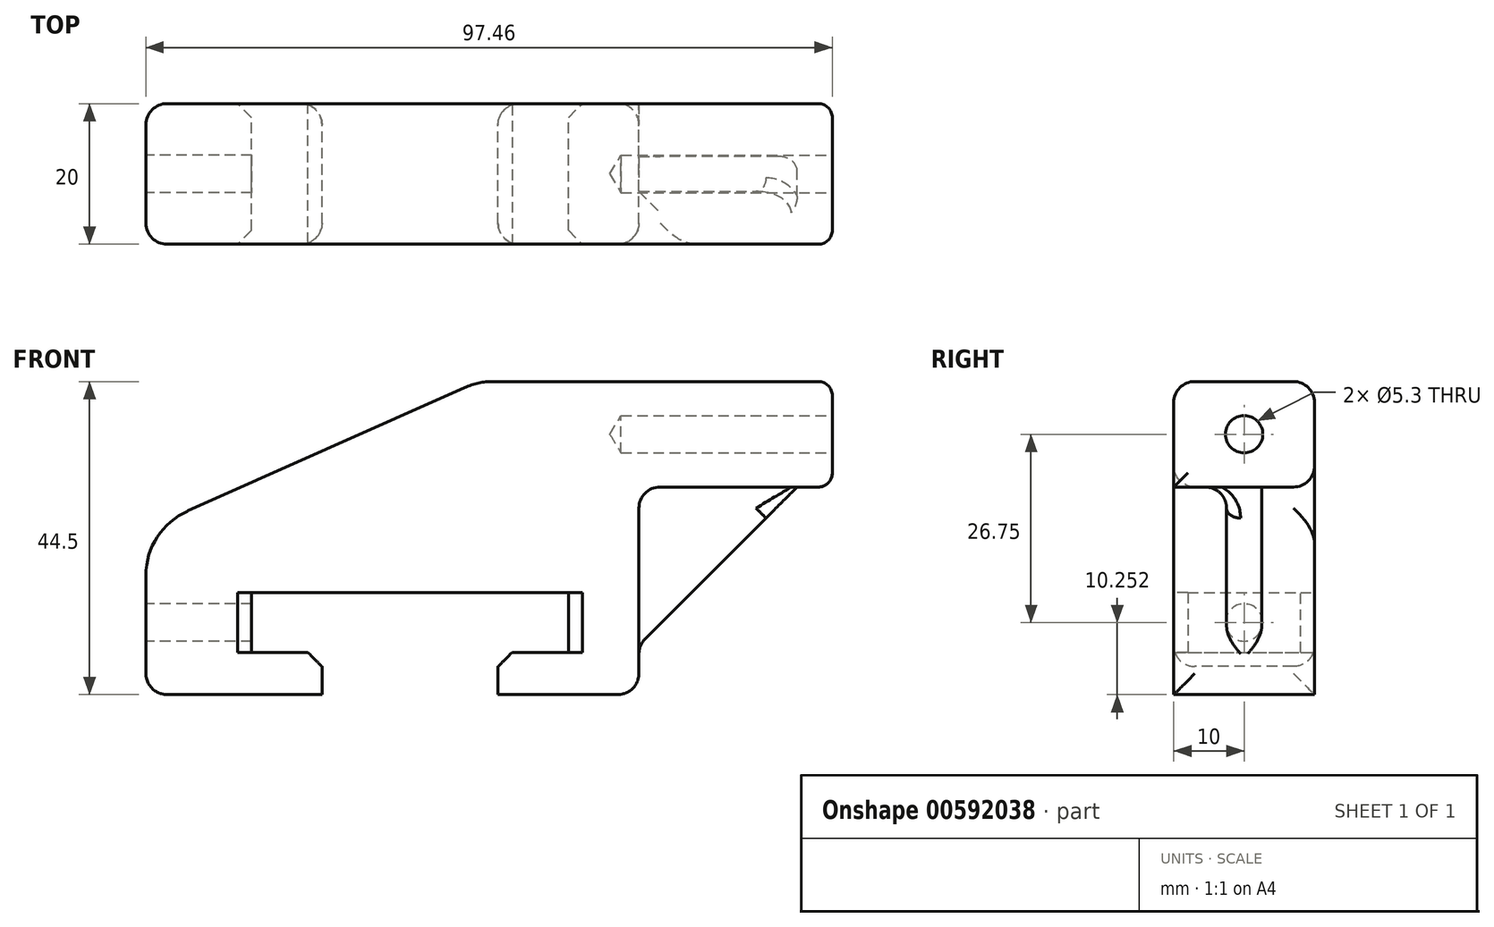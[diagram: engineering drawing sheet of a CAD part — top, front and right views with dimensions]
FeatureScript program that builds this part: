
annotation { "Feature Type Name" : "Feature", "Feature Type Description" : "" }
export const myFeature = defineFeature(function(context is Context, id is Id, definition is map)
    precondition{}
    {
        {
            var Q0;
            Q0=qCreatedBy(makeId("Front.planeOp"),FACE);
            var sketch = newSketch(context, id + "F0", { "sketchPlane" : qUnion([Q0])});
            skLineSegment(sketch, "E0", {"start": v(-69.54, -2.42) * mm, "end": v(-69.54, -25.86) * mm});
            skLineSegment(sketch, "E1", {"start": v(-69.54, -25.86) * mm, "end": v(-44.54, -25.86) * mm});
            skLineSegment(sketch, "E2", {"start": v(-44.54, -25.86) * mm, "end": v(-44.54, -19.86) * mm});
            skLineSegment(sketch, "E3", {"start": v(-44.54, -19.86) * mm, "end": v(-54.54, -19.86) * mm});
            skLineSegment(sketch, "E4", {"start": v(-54.54, -19.86) * mm, "end": v(-54.54, -11.36) * mm});
            skLineSegment(sketch, "E5", {"start": v(-54.54, -11.36) * mm, "end": v(-44.54, -11.36) * mm});
            skLineSegment(sketch, "E6", {"start": v(-44.54, -11.36) * mm, "end": v(-9.54, -11.36) * mm});
            skLineSegment(sketch, "E7", {"start": v(-9.54, -11.36) * mm, "end": v(-9.54, -19.86) * mm});
            skLineSegment(sketch, "E8", {"start": v(-9.54, -19.86) * mm, "end": v(-19.54, -19.86) * mm});
            skLineSegment(sketch, "E9", {"start": v(-19.54, -19.86) * mm, "end": v(-19.54, -25.86) * mm});
            skLineSegment(sketch, "E10", {"start": v(-19.54, -25.86) * mm, "end": v(0.46, -25.86) * mm});
            skLineSegment(sketch, "E11", {"start": v(0.46, -25.86) * mm, "end": v(0.46, 3.64) * mm});
            skLineSegment(sketch, "E12", {"start": v(0.46, 3.64) * mm, "end": v(22.92, 3.64) * mm});
            skLineSegment(sketch, "E13", {"start": v(22.92, 3.64) * mm, "end": v(22.92, 18.64) * mm});
            skLineSegment(sketch, "E14", {"start": v(22.92, 18.64) * mm, "end": v(-22.34, 18.64) * mm});
            skLineSegment(sketch, "E15", {"start": v(-80.76, -15.6) * mm, "end": v(-46.79, -15.6) * mm, "construction": true});
            skPoint(sketch, "E15.startSnap0", {"position": v(-54.54, -15.6) * mm});
            skLineSegment(sketch, "E16", {"start": v(26.63, 11.14) * mm, "end": v(-61.45, 11.14) * mm, "construction": true});
            skPoint(sketch, "E17", {"position": v(-69.54, -2.42) * mm});
            skPoint(sketch, "E18", {"position": v(-22.34, 18.64) * mm});
            skLineSegment(sketch, "E19", {"start": v(-69.54, -2.42) * mm, "end": v(-22.34, 18.64) * mm});
            skSolve(sketch);
        }
        {
            var Q0;
            Q0=makeQuery(id+"F0.imprint","IMPRINT",FACE,{"disambiguationData":[TD([[makeQuery(id+"F0.imprint","IMPRINT",EDGE,{"derivedFrom":sQuery(id+"F0.wireOp",EDGE,"E0")}),1.0]])]});
            extrude(context, id + "F1", {"entities" : qUnion([Q0]), "endBound" : BoundingType.SYMMETRIC, "depth" : 20 * mm, "offsetDistance" : 25 * mm});
        }
        {
            var Q0;
            Q0=makeQuery(id+"F1.opExtrude","SWEPT_FACE",FACE,{"disambiguationData":[OSD([sQuery(id+"F0.wireOp",EDGE,"E0")])]});
            var sketch = newSketch(context, id + "F2", { "sketchPlane" : qUnion([Q0])});
            skPoint(sketch, "E20", {"position": v(0, -15.6) * mm});
            skSolve(sketch);
        }
        {
            var Q0;
            Q0=makeQuery(id+"F1.opExtrude","SWEPT_FACE",FACE,{"disambiguationData":[OSD([sQuery(id+"F0.wireOp",EDGE,"E13")])]});
            var sketch = newSketch(context, id + "F3", { "sketchPlane" : qUnion([Q0])});
            skPoint(sketch, "E21", {"position": v(0, 11.14) * mm});
            skSolve(sketch);
        }
        {
            var Q0;
            Q0=sQuery(id+"F3.wireOp",VERTEX,"E21");
            var Q1;
            Q1=makeQuery(id+"F1.opExtrude","SWEPT_BODY",BODY,{"disambiguationData":[OSD([sQuery(id+"F0.wireOp",EDGE,"E0"),sQuery(id+"F0.wireOp",EDGE,"E1"),sQuery(id+"F0.wireOp",EDGE,"E2"),sQuery(id+"F0.wireOp",EDGE,"E3"),sQuery(id+"F0.wireOp",EDGE,"E4"),sQuery(id+"F0.wireOp",EDGE,"E5"),sQuery(id+"F0.wireOp",EDGE,"E6"),sQuery(id+"F0.wireOp",EDGE,"E7"),sQuery(id+"F0.wireOp",EDGE,"E8"),sQuery(id+"F0.wireOp",EDGE,"E9"),sQuery(id+"F0.wireOp",EDGE,"E10"),sQuery(id+"F0.wireOp",EDGE,"E11"),sQuery(id+"F0.wireOp",EDGE,"E12"),sQuery(id+"F0.wireOp",EDGE,"E13"),sQuery(id+"F0.wireOp",EDGE,"E14"),sQuery(id+"F0.wireOp",EDGE,"E19")])]});
            hole(context, id + "F4", {"style" : HoleStyle.SIMPLE, "endStyle" : HoleEndStyle.BLIND, "holeDiameter" : 5.3 * mm, "majorDiameter" : 5 * mm, "holeDepth" : 25 * mm, "isTappedThrough" : true, "tappedDepth" : 12 * mm, "tapClearance" : 3, "locations" : qUnion([Q0]), "scope" : qUnion([Q1])});
        }
        {
            var Q0;
            Q0=sQuery(id+"F2.wireOp",VERTEX,"E20");
            var Q1;
            Q1=makeQuery(id+"F1.opExtrude","SWEPT_BODY",BODY,{"disambiguationData":[OSD([sQuery(id+"F0.wireOp",EDGE,"E0"),sQuery(id+"F0.wireOp",EDGE,"E1"),sQuery(id+"F0.wireOp",EDGE,"E2"),sQuery(id+"F0.wireOp",EDGE,"E3"),sQuery(id+"F0.wireOp",EDGE,"E4"),sQuery(id+"F0.wireOp",EDGE,"E5"),sQuery(id+"F0.wireOp",EDGE,"E6"),sQuery(id+"F0.wireOp",EDGE,"E7"),sQuery(id+"F0.wireOp",EDGE,"E8"),sQuery(id+"F0.wireOp",EDGE,"E9"),sQuery(id+"F0.wireOp",EDGE,"E10"),sQuery(id+"F0.wireOp",EDGE,"E11"),sQuery(id+"F0.wireOp",EDGE,"E12"),sQuery(id+"F0.wireOp",EDGE,"E13"),sQuery(id+"F0.wireOp",EDGE,"E14"),sQuery(id+"F0.wireOp",EDGE,"E19")])]});
            hole(context, id + "F5", {"style" : HoleStyle.SIMPLE, "endStyle" : HoleEndStyle.BLIND, "holeDiameter" : 5.3 * mm, "majorDiameter" : 5 * mm, "holeDepth" : 25 * mm, "isTappedThrough" : true, "tappedDepth" : 12 * mm, "tapClearance" : 3, "locations" : qUnion([Q0]), "scope" : qUnion([Q1])});
        }
        {
            var Q0;
            Q0=makeQuery(id+"F1.opExtrude","SWEPT_FACE",FACE,{"disambiguationData":[OSD([sQuery(id+"F0.wireOp",EDGE,"E12")])]});
            var sketch = newSketch(context, id + "F6", { "sketchPlane" : qUnion([Q0])});
            skLineSegment(sketch, "E22", {"start": v(0.46, 2.5) * mm, "end": v(22.92, 2.5) * mm});
            skLineSegment(sketch, "E23", {"start": v(22.92, 2.5) * mm, "end": v(22.92, -2.5) * mm});
            skLineSegment(sketch, "E24", {"start": v(22.92, -2.5) * mm, "end": v(0.46, -2.5) * mm});
            skLineSegment(sketch, "E25", {"start": v(0.46, -2.5) * mm, "end": v(0.46, 2.5) * mm});
            skSolve(sketch);
        }
        {
            var Q0;
            Q0=makeQuery(id+"F6.imprint","IMPRINT",FACE,{"disambiguationData":[TD([[makeQuery(id+"F6.imprint","IMPRINT",EDGE,{"derivedFrom":sQuery(id+"F6.wireOp",EDGE,"E22")}),-1.0]])]});
            extrude(context, id + "F7", {"entities" : qUnion([Q0]), "operationType" : NewBodyOperationType.ADD, "depth" : 29 * mm, "offsetDistance" : 25 * mm});
        }
        {
            var Q0;
            Q0=makeQuery(id+"F7.opExtrude","CAP_EDGE",EDGE,{"disambiguationData":[OSD([sQuery(id+"F6.wireOp",EDGE,"E23")])],"isStart":false});
            chamfer(context, id + "F8", {"entities" : qUnion([Q0]), "chamferType" : ChamferType.TWO_OFFSETS, "width1" : 29 * mm, "oppositeDirection" : false, "width2" : 29 * mm, "tangentPropagation" : true});
        }
        {
            var Q0;
            {var subQ0=sQuery(id+"F0.wireOp",EDGE,"E12");var subQ1=sQuery(id+"F0.wireOp",EDGE,"E11");Q0=makeQuery(id+"F7.boolean.opBoolean","SPLIT",EDGE,{"disambiguationData":[TD([makeQuery(id+"F7.opExtrude","SWEPT_FACE",FACE,{"disambiguationData":[OSD([sQuery(id+"F6.wireOp",EDGE,"E24")])]})])],"derivedFrom":makeQuery(id+"F1.opExtrude","SWEPT_EDGE",EDGE,{"disambiguationData":[OSD([subQ1,subQ0])]})});}
            var Q1;
            {var subQ0=sQuery(id+"F0.wireOp",EDGE,"E12");var subQ1=sQuery(id+"F0.wireOp",EDGE,"E11");Q1=makeQuery(id+"F7.boolean.opBoolean","SPLIT",EDGE,{"disambiguationData":[TD([makeQuery(id+"F7.opExtrude","SWEPT_FACE",FACE,{"disambiguationData":[OSD([sQuery(id+"F6.wireOp",EDGE,"E22")])]})])],"derivedFrom":makeQuery(id+"F1.opExtrude","SWEPT_EDGE",EDGE,{"disambiguationData":[OSD([subQ1,subQ0])]})});}
            var Q2;
            Q2=makeQuery(id+"F7.opExtrude","SWEPT_EDGE",EDGE,{"disambiguationData":[OSD([sQuery(id+"F0.wireOp",EDGE,"E11"),sQuery(id+"F0.wireOp",EDGE,"E12"),sQuery(id+"F6.wireOp",EDGE,"E22"),sQuery(id+"F6.wireOp",EDGE,"E25")])]});
            var Q3;
            Q3=makeQuery(id+"F7.opExtrude","CAP_EDGE",EDGE,{"disambiguationData":[OSD([sQuery(id+"F6.wireOp",EDGE,"E22")])],"isStart":true});
            var Q4;
            Q4=makeQuery(id+"F7.opExtrude","CAP_EDGE",EDGE,{"disambiguationData":[OSD([sQuery(id+"F6.wireOp",EDGE,"E24")])],"isStart":true});
            var Q5;
            Q5=makeQuery(id+"F7.opExtrude","SWEPT_EDGE",EDGE,{"disambiguationData":[OSD([sQuery(id+"F0.wireOp",EDGE,"E11"),sQuery(id+"F0.wireOp",EDGE,"E12"),sQuery(id+"F6.wireOp",EDGE,"E24"),sQuery(id+"F6.wireOp",EDGE,"E25")])]});
            var Q6;
            Q6=makeQuery(id+"F8.opChamfer","BLEND_EDGE",EDGE,{"blendedFrom":[makeQuery(id+"F7.opExtrude","CAP_EDGE",EDGE,{"disambiguationData":[OSD([sQuery(id+"F6.wireOp",EDGE,"E23")])],"isStart":false}),makeQuery(id+"F1.opExtrude","SWEPT_FACE",FACE,{"disambiguationData":[OSD([sQuery(id+"F0.wireOp",EDGE,"E11")])]})],"blendedInto":[makeQuery(id+"F1.opExtrude","SWEPT_FACE",FACE,{"disambiguationData":[OSD([sQuery(id+"F0.wireOp",EDGE,"E11")])]})]});
            var Q7;
            Q7=makeQuery(id+"F1.opExtrude","CAP_EDGE",EDGE,{"disambiguationData":[OSD([sQuery(id+"F0.wireOp",EDGE,"E12")])],"isStart":true});
            var Q8;
            Q8=makeQuery(id+"F1.opExtrude","CAP_EDGE",EDGE,{"disambiguationData":[OSD([sQuery(id+"F0.wireOp",EDGE,"E11")])],"isStart":false});
            var Q9;
            Q9=makeQuery(id+"F1.opExtrude","CAP_EDGE",EDGE,{"disambiguationData":[OSD([sQuery(id+"F0.wireOp",EDGE,"E14")])],"isStart":true});
            var Q10;
            Q10=makeQuery(id+"F1.opExtrude","CAP_EDGE",EDGE,{"disambiguationData":[OSD([sQuery(id+"F0.wireOp",EDGE,"E19")])],"isStart":true});
            var Q11;
            Q11=makeQuery(id+"F1.opExtrude","CAP_EDGE",EDGE,{"disambiguationData":[OSD([sQuery(id+"F0.wireOp",EDGE,"E19")])],"isStart":false});
            var Q12;
            Q12=makeQuery(id+"F1.opExtrude","CAP_EDGE",EDGE,{"disambiguationData":[OSD([sQuery(id+"F0.wireOp",EDGE,"E14")])],"isStart":false});
            var Q13;
            Q13=makeQuery(id+"F1.opExtrude","CAP_EDGE",EDGE,{"disambiguationData":[OSD([sQuery(id+"F0.wireOp",EDGE,"E0")])],"isStart":false});
            var Q14;
            Q14=makeQuery(id+"F1.opExtrude","CAP_EDGE",EDGE,{"disambiguationData":[OSD([sQuery(id+"F0.wireOp",EDGE,"E0")])],"isStart":true});
            var Q15;
            Q15=makeQuery(id+"F1.opExtrude","SWEPT_EDGE",EDGE,{"disambiguationData":[OSD([sQuery(id+"F0.wireOp",EDGE,"E0"),sQuery(id+"F0.wireOp",EDGE,"E1")])]});
            var Q16;
            Q16=makeQuery(id+"F1.opExtrude","SWEPT_EDGE",EDGE,{"disambiguationData":[OSD([sQuery(id+"F0.wireOp",EDGE,"E10"),sQuery(id+"F0.wireOp",EDGE,"E11")])]});
            var Q17;
            Q17=makeQuery(id+"F1.opExtrude","CAP_EDGE",EDGE,{"disambiguationData":[OSD([sQuery(id+"F0.wireOp",EDGE,"E2")])],"isStart":false});
            var Q18;
            Q18=makeQuery(id+"F1.opExtrude","CAP_EDGE",EDGE,{"disambiguationData":[OSD([sQuery(id+"F0.wireOp",EDGE,"E9")])],"isStart":false});
            var Q19;
            Q19=makeQuery(id+"F1.opExtrude","CAP_EDGE",EDGE,{"disambiguationData":[OSD([sQuery(id+"F0.wireOp",EDGE,"E9")])],"isStart":true});
            var Q20;
            Q20=makeQuery(id+"F1.opExtrude","CAP_EDGE",EDGE,{"disambiguationData":[OSD([sQuery(id+"F0.wireOp",EDGE,"E2")])],"isStart":true});
            fillet(context, id + "F9", {"entities" : qUnion([Q0, Q1, Q2, Q3, Q4, Q5, Q6, Q7, Q8, Q9, Q10, Q11, Q12, Q13, Q14, Q15, Q16, Q17, Q18, Q19, Q20]), "radius" : 3 * mm, "tangentPropagation" : true, "allowEdgeOverflow" : false});
        }
        {
            var Q0;
            Q0=makeQuery(id+"F7.boolean.opBoolean","MERGE",FACE,{"derivedFrom":[makeQuery(id+"F1.opExtrude","SWEPT_FACE",FACE,{"disambiguationData":[OSD([sQuery(id+"F0.wireOp",EDGE,"E13")])]}),makeQuery(id+"F7.opExtrude","SWEPT_FACE",FACE,{"disambiguationData":[OSD([sQuery(id+"F6.wireOp",EDGE,"E23")])]})]});
            extrude(context, id + "F10", {"entities" : qUnion([Q0]), "operationType" : NewBodyOperationType.ADD, "depth" : 5 * mm, "offsetDistance" : 25 * mm});
        }
        {
            var Q0;
            Q0=makeQuery(id+"F8.opChamfer","BLEND_EDGE",EDGE,{"blendedFrom":[makeQuery(id+"F7.opExtrude","CAP_EDGE",EDGE,{"disambiguationData":[OSD([sQuery(id+"F6.wireOp",EDGE,"E23")])],"isStart":false}),makeQuery(id+"F7.opExtrude","SWEPT_FACE",FACE,{"disambiguationData":[OSD([sQuery(id+"F6.wireOp",EDGE,"E24")])]})],"blendedInto":[makeQuery(id+"F7.opExtrude","SWEPT_FACE",FACE,{"disambiguationData":[OSD([sQuery(id+"F6.wireOp",EDGE,"E24")])]})]});
            var Q1;
            Q1=makeQuery(id+"F8.opChamfer","BLEND_EDGE",EDGE,{"blendedFrom":[makeQuery(id+"F7.opExtrude","CAP_EDGE",EDGE,{"disambiguationData":[OSD([sQuery(id+"F6.wireOp",EDGE,"E23")])],"isStart":false}),makeQuery(id+"F7.opExtrude","SWEPT_FACE",FACE,{"disambiguationData":[OSD([sQuery(id+"F6.wireOp",EDGE,"E22")])]})],"blendedInto":[makeQuery(id+"F7.opExtrude","SWEPT_FACE",FACE,{"disambiguationData":[OSD([sQuery(id+"F6.wireOp",EDGE,"E22")])]})]});
            var Q2;
            {var subQ0=sQuery(id+"F6.wireOp",EDGE,"E23");var subQ1=makeQuery(id+"F7.opExtrude","SWEPT_FACE",FACE,{"disambiguationData":[OSD([subQ0])]});var subQ2=sQuery(id+"F0.wireOp",EDGE,"E13");var subQ3=makeQuery(id+"F1.opExtrude","SWEPT_FACE",FACE,{"disambiguationData":[OSD([subQ2])]});var subQ4=sQuery(id+"F0.wireOp",EDGE,"E12");var subQ20=makeQuery(id+"F1.opExtrude","SWEPT_EDGE",EDGE,{"disambiguationData":[OSD([subQ4,subQ2])]});Q2=makeQuery(id+"F10.opExtrude","CAP_EDGE",EDGE,{"disambiguationData":[OSD([subQ4,subQ2,subQ0]),TDD([makeQuery(id+"F7.boolean.opBoolean","SPLIT",EDGE,{"disambiguationData":[TD([makeQuery(id+"F7.opExtrude","SWEPT_FACE",FACE,{"disambiguationData":[OSD([sQuery(id+"F6.wireOp",EDGE,"E24")])]})])],"derivedFrom":subQ20}),makeQuery(id+"F7.boolean.opBoolean","SPLIT",EDGE,{"disambiguationData":[TD([makeQuery(id+"F7.opExtrude","SWEPT_FACE",FACE,{"disambiguationData":[OSD([sQuery(id+"F6.wireOp",EDGE,"E22")])]})])],"derivedFrom":subQ20}),makeQuery(id+"F8.opChamfer","BLEND_EDGE",EDGE,{"blendedFrom":[makeQuery(id+"F7.opExtrude","CAP_EDGE",EDGE,{"disambiguationData":[OSD([subQ0])],"isStart":false}),makeQuery(id+"F7.boolean.opBoolean","MERGE",FACE,{"derivedFrom":[subQ3,subQ1]})],"blendedInto":[makeQuery(id+"F7.boolean.opBoolean","MERGE",FACE,{"derivedFrom":[subQ3,subQ1]})]})])],"isStart":false});}
            fillet(context, id + "F11", {"entities" : qUnion([Q0, Q1, Q2]), "radius" : 2 * mm, "tangentPropagation" : true, "allowEdgeOverflow" : false});
        }
        {
            var Q0;
            Q0=makeQuery(id+"F1.opExtrude","SWEPT_EDGE",EDGE,{"disambiguationData":[OSD([sQuery(id+"F0.wireOp",EDGE,"E8"),sQuery(id+"F0.wireOp",EDGE,"E9")])]});
            var Q1;
            Q1=makeQuery(id+"F1.opExtrude","SWEPT_EDGE",EDGE,{"disambiguationData":[OSD([sQuery(id+"F0.wireOp",EDGE,"E2"),sQuery(id+"F0.wireOp",EDGE,"E3")])]});
            var Q2;
            Q2=makeQuery(id+"F1.opExtrude","CAP_EDGE",EDGE,{"disambiguationData":[OSD([sQuery(id+"F0.wireOp",EDGE,"E7")])],"isStart":true});
            var Q3;
            Q3=makeQuery(id+"F1.opExtrude","CAP_EDGE",EDGE,{"disambiguationData":[OSD([sQuery(id+"F0.wireOp",EDGE,"E4")])],"isStart":true});
            var Q4;
            Q4=makeQuery(id+"F1.opExtrude","CAP_EDGE",EDGE,{"disambiguationData":[OSD([sQuery(id+"F0.wireOp",EDGE,"E7")])],"isStart":false});
            var Q5;
            Q5=makeQuery(id+"F1.opExtrude","CAP_EDGE",EDGE,{"disambiguationData":[OSD([sQuery(id+"F0.wireOp",EDGE,"E4")])],"isStart":false});
            chamfer(context, id + "F12", {"entities" : qUnion([Q0, Q1, Q2, Q3, Q4, Q5]), "width" : 2 * mm});
        }
        {
            var Q0;
            Q0=makeQuery(id+"F1.opExtrude","SWEPT_EDGE",EDGE,{"disambiguationData":[OSD([sQuery(id+"F0.wireOp",EDGE,"E0"),sQuery(id+"F0.wireOp",EDGE,"E19")])]});
            var Q1;
            Q1=makeQuery(id+"F1.opExtrude","SWEPT_EDGE",EDGE,{"disambiguationData":[OSD([sQuery(id+"F0.wireOp",EDGE,"E14"),sQuery(id+"F0.wireOp",EDGE,"E19")])]});
            fillet(context, id + "F13", {"entities" : qUnion([Q0, Q1]), "radius" : 10 * mm, "tangentPropagation" : true, "allowEdgeOverflow" : false});
        }
    });
